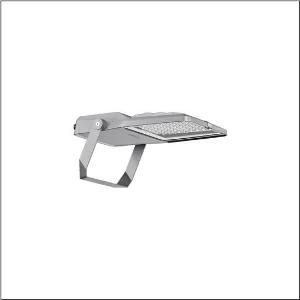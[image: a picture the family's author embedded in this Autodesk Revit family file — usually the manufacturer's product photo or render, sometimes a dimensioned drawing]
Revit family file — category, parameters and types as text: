
# Revit family: floodlight_fl_21_iq_mini___pl64_5xa7772d2e1a_f3f3
name_source: partatom
category: Lighting Fixtures
units: mm (PartAtom-declared; Revit-internal decimal feet)

## family parameters
Cut with Voids When Loaded = No
Host = Face
Light Source = No
Part Type = Normal
Room Calculation Point = No
Round Connector Dimension = Use Diameter
Shared = No

## types (1)
- --- (1 x LED, 17220 lm, 143 W, 3000K)
    Apparent Load = 143 VA
    CIE Flux Codes = 28 80 98 100 100
    Color Rendering = 70
    Color Temperature = 3000K
    Default Elevation = 1800 mm
    Description = Floodlight FL 21 iQ mini, floodlight, primary light control with lens, of PMMA, primary optical cover: protective disc, of toughened safety glass, transparent, light distribution: PL64, light emission: direct distribution, installation type: surface-mounted, LED, High Power LED, rated luminous flux: 17.220lm, luminous efficacy: 120lm/W, light colour: 730, colour temperature: 3000K, control: Street-Remote, Auto-Match, Temp-Guard, Night-Set, Smart-Wire, Desk-Remote (wireless, voltage-free reading and setting of iQ features in the workshop via application-optimized NFC function/RFID function), optimised constant luminous flux control (CLO 2.0), with terminal, 6-pole, mains connection: 220..240V, AC, 50/60Hz, start of lifetime: 143W, end of service life: 152W, reduction: 61W, luminaire housing, of diecast aluminium, powder-coated, Siteco® metallic grey (DB 702S), corrosivity category C5 mid according to DIN EN ISO 12944, sealing non-destructively replaceable, mounting bracket, of steel, galvanised, powder-coated, Siteco® metallic grey (DB 702S), protection rating (complete): IP66, insulation class (complete): insulation class II (safety insulation), certification: CE, ENEC, VDE, protection symbol: D, impact resistance: IK08, permissible operating ambient temperature: -40..+40°C, permissible operating ambient temperature for outdoor applications: -40..+50°C, standard: DIN EN 12944, LABS conformity tested according to VDMA 24364:2018-05, packaging unit: 1 piece

Light Distribution: PL64
    Height = 70 mm
    Lamp = 1 x LED
    Lamp Light Flux = 17220 lm
    Lamp Power = 143 W
    Lamp count = 1
    Length = 485 mm
    Luminous efficacy = 120 lm/W
    Manufacturer = Siteco
    ModVariant = No
    Model = 5XA7772D2E1A
    Number of Poles = 1
    OnlyDefault = Yes
    Power Factor = 1
    Product Name = Floodlight FL 21 iQ mini | PL64
    Product group = floodlight | pylon annexe
    ProductGroupID = 6200
    Protection Class = Protection class II
    Protection Degree = IP 66
    RLX_Detail_Level = 1
    RLX_Emergency_Light_Flux = 0 lm
    RLX_Emergency_Type = 0
    RLX_Emergency_Type_DB = No
    RlxData = <blob elided: 96513 chars, md5=c3ea560d>
    Socket = socket
    Standby Power = 0 W
    System Light Flux = 17220 lm
    System Power = 143 W
    Type Comments = factory setting: luminous flux: 100 % | dim-lin: 254 | 730 mA
    Type Image = l_1006845.jpg
    URL = http://relux.com
    VarID = @adj_098177
    Voltage = 0 V
    Weight = 0.00 kg
    Width = 337 mm

## geometry (parser evidence)
native form markers: Blend x4, Sweep x14
no freeform markers — native parametric forms only
